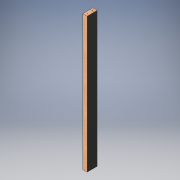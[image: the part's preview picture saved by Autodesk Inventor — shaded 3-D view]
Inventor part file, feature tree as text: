
AUTODESK INVENTOR PART (.ipt)
format: ipt  version: 2017 (Build 210142000, 142)  size: 123,904 bytes
history: native  units: in
note: dims shown in document units (in); Inventor stores cm internally (conversion verified against a paired STEP export)
features: extrude x3, sketch x3
ambient origin geometry x8: Origin, YZ Plane, XZ Plane, XY Plane, X Axis, Y Axis, Z Axis, Center Point
bodies: Solid1 (feature_tree)
feature tree (6):
  extrude  "Wood"  Depth=3.5in
  extrude  "Extrusion4"  Depth=46.5in
  extrude  "Extrusion5"  Depth=1.5in
  sketch  "Sketch1"  dims[d0=1.5in d1=3.5in]
  sketch  "Sketch4"  dims[d2=46.5in d3=0.0in d11=0.1875in]
  sketch  "Sketch5"  dims[d12=1.5in d13=0.0in d14=1.5in d15=0.1875in d16=1.5in d17=0.0in]
